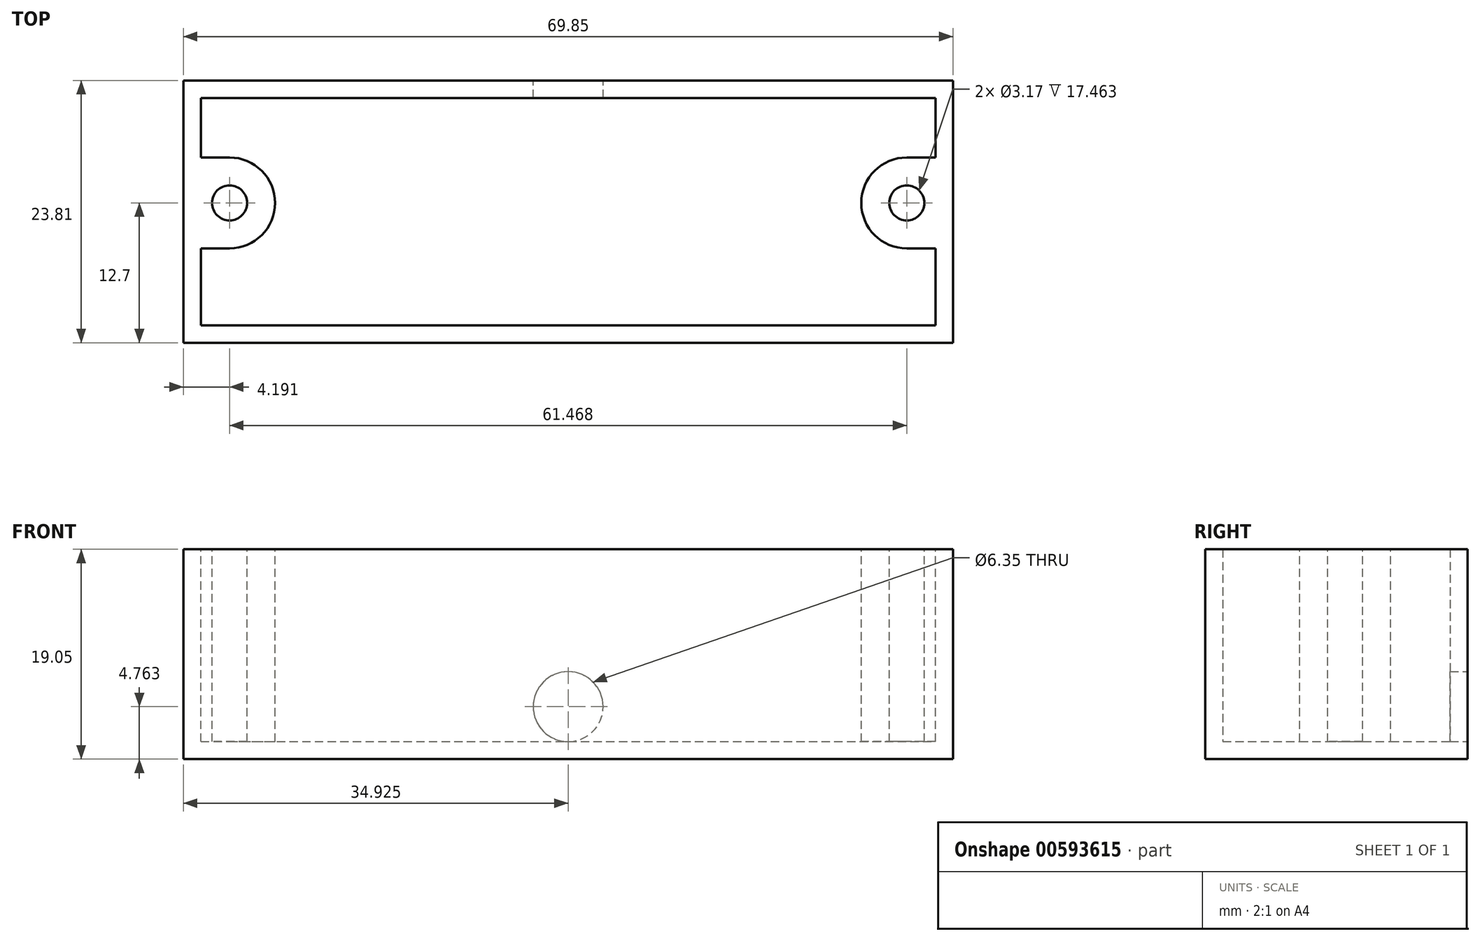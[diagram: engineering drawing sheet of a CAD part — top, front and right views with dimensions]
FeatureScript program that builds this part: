
annotation { "Feature Type Name" : "Feature", "Feature Type Description" : "" }
export const myFeature = defineFeature(function(context is Context, id is Id, definition is map)
    precondition{}
    {
        {
            assignVariable(context, id + "F0", {"variableType" : VariableType.LENGTH, "name" : "height", "lengthValue" : 19.05 * mm});
        }
        {
            var Q0;
            Q0=qCreatedBy(makeId("Top.planeOp"),FACE);
            var sketch = newSketch(context, id + "F1", { "sketchPlane" : qUnion([Q0])});
            skLineSegment(sketch, "E0.bottom", {"start": v(0, 0) * mm, "end": v(69.85, 0) * mm});
            skLineSegment(sketch, "E0.top", {"start": v(0, 23.81) * mm, "end": v(69.85, 23.81) * mm});
            skLineSegment(sketch, "E0.left", {"start": v(0, 0) * mm, "end": v(0, 23.81) * mm});
            skLineSegment(sketch, "E0.right", {"start": v(69.85, 0) * mm, "end": v(69.85, 23.81) * mm});
            skSolve(sketch);
        }
        {
            var Q0;
            Q0=makeQuery(id+"F1.imprint","IMPRINT",FACE,{"disambiguationData":[TD([[makeQuery(id+"F1.imprint","IMPRINT",EDGE,{"derivedFrom":sQuery(id+"F1.wireOp",EDGE,"E0.bottom")}),1.0]])]});
            extrude(context, id + "F2", {"entities" : qUnion([Q0]), "depth" : getVariable(context, 'height'), "offsetDistance" : 25.4 * mm});
        }
        {
            var Q0;
            Q0=makeQuery(id+"F2.opExtrude","CAP_FACE",FACE,{"disambiguationData":[OSD([sQuery(id+"F1.wireOp",EDGE,"E0.bottom"),sQuery(id+"F1.wireOp",EDGE,"E0.top"),sQuery(id+"F1.wireOp",EDGE,"E0.left"),sQuery(id+"F1.wireOp",EDGE,"E0.right")])],"isStart":false});
            shell(context, id + "F3", {"entities" : qUnion([Q0]), "thickness" : 1.59 * mm});
        }
        {
            var Q0;
            Q0=makeQuery(id+"F2.opExtrude","CAP_FACE",FACE,{"disambiguationData":[OSD([sQuery(id+"F1.wireOp",EDGE,"E0.bottom"),sQuery(id+"F1.wireOp",EDGE,"E0.top"),sQuery(id+"F1.wireOp",EDGE,"E0.left"),sQuery(id+"F1.wireOp",EDGE,"E0.right")])],"isStart":false});
            var sketch = newSketch(context, id + "F4", { "sketchPlane" : qUnion([Q0])});
            skLineSegment(sketch, "E1", {"start": v(34.93, 23.81) * mm, "end": v(34.93, 0) * mm, "construction": true});
            skLineSegment(sketch, "E2.0", {"start": v(4.2, 25.4) * mm, "end": v(4.2, 0) * mm, "construction": true});
            skCircle(sketch, "E3", {"center": v(4.2, 12.7) * mm, "radius": 1.59 * mm});
            skArc(sketch, "E4.0", {"start": v(4.2, 8.57) * mm, "mid": v(8.32, 12.7) * mm, "end": v(4.2, 16.83) * mm});
            skLineSegment(sketch, "E5", {"start": v(4.2, 16.83) * mm, "end": v(1.59, 16.83) * mm});
            skLineSegment(sketch, "E6", {"start": v(4.2, 8.57) * mm, "end": v(1.59, 8.57) * mm});
            skLineSegment(sketch, "E7.MirrorCS", {"start": v(65.66, 8.57) * mm, "end": v(68.26, 8.57) * mm});
            skLineSegment(sketch, "E8.MirrorCS", {"start": v(65.66, 16.83) * mm, "end": v(68.26, 16.83) * mm});
            skPoint(sketch, "E9.MirrorP", {"position": v(65.66, 12.7) * mm});
            skCircle(sketch, "E10.MirrorC", {"center": v(65.66, 12.7) * mm, "radius": 1.59 * mm});
            skArc(sketch, "E11.MirrorCS", {"start": v(65.66, 8.57) * mm, "mid": v(61.53, 12.7) * mm, "end": v(65.66, 16.83) * mm});
            skSolve(sketch);
        }
        {
            var Q0;
            Q0=makeQuery(id+"F4.imprint","IMPRINT",FACE,{"disambiguationData":[TD([[makeQuery(id+"F4.imprint","IMPRINT",EDGE,{"derivedFrom":sQuery(id+"F4.wireOp",EDGE,"E3")}),-1.0]])]});
            var Q1;
            {var subQ1=sQuery(id+"F4.wireOp",EDGE,"E7.MirrorCS");Q1=makeQuery(id+"F4.imprint","IMPRINT",FACE,{"disambiguationData":[TD([[makeQuery(id+"F4.imprint","IMPRINT",EDGE,{"derivedFrom":subQ1}),1.0]])]});}
            var Q2;
            Q2=makeQuery(id+"F3.opShell","OFFSET_FACE",FACE,{"disambiguationData":[OSD([sQuery(id+"F1.wireOp",EDGE,"E0.bottom"),sQuery(id+"F1.wireOp",EDGE,"E0.top"),sQuery(id+"F1.wireOp",EDGE,"E0.left"),sQuery(id+"F1.wireOp",EDGE,"E0.right")])]});
            extrude(context, id + "F5", {"entities" : qUnion([Q0, Q1]), "operationType" : NewBodyOperationType.ADD, "endBound" : BoundingType.UP_TO_SURFACE, "oppositeDirection" : true, "depth" : 25.4 * mm, "endBoundEntityFace" : qUnion([Q2]), "offsetDistance" : 25.4 * mm});
        }
        {
            var Q0;
            Q0=makeQuery(id+"F2.opExtrude","SWEPT_FACE",FACE,{"disambiguationData":[OSD([sQuery(id+"F1.wireOp",EDGE,"E0.top")])]});
            var sketch = newSketch(context, id + "F6", { "sketchPlane" : qUnion([Q0])});
            skCircle(sketch, "E12", {"center": v(-34.93, 4.76) * mm, "radius": 3.18 * mm});
            skLineSegment(sketch, "E13", {"start": v(-34.93, 19.05) * mm, "end": v(-34.93, 0) * mm, "construction": true});
            skSolve(sketch);
        }
        {
            var Q0;
            Q0=makeQuery(id+"F6.imprint","IMPRINT",FACE,{"disambiguationData":[TD([[makeQuery(id+"F6.imprint","IMPRINT",EDGE,{"derivedFrom":sQuery(id+"F6.wireOp",EDGE,"E12")}),1.0]])]});
            var Q1;
            Q1=makeQuery(id+"F3.opShell","OFFSET_FACE",FACE,{"disambiguationData":[OSD([sQuery(id+"F1.wireOp",EDGE,"E0.top")])]});
            extrude(context, id + "F7", {"entities" : qUnion([Q0]), "operationType" : NewBodyOperationType.REMOVE, "endBound" : BoundingType.UP_TO_SURFACE, "oppositeDirection" : true, "depth" : 25.4 * mm, "endBoundEntityFace" : qUnion([Q1]), "offsetDistance" : 25.4 * mm});
        }
    });
